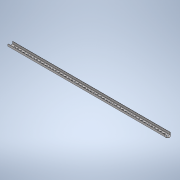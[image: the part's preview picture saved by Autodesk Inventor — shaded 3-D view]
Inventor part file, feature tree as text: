
AUTODESK INVENTOR PART (.ipt)
format: ipt  version: 2022 (Build 260153000, 153)  size: 299,008 bytes
history: native  units: mm
features: sheet_metal_op x4, sketch x4, other x3, extrude x2, pattern_linear x1
ambient origin geometry x8: Origin, YZ Plane, XZ Plane, XY Plane, X Axis, Y Axis, Z Axis, Center Point
bodies: Solid1 (feature_tree)
feature tree (14):
  sheet_metal_op  "Face1"
  sheet_metal_op  "Flange1"
  extrude  "Extrusion1"  Depth=30.0mm
  pattern_linear  "Rectangular Pattern1"  Spacing1=3.0mm  [1 undecoded]
  extrude  "Extrusion2"  Depth=1.5mm
  sketch  "Sketch1"  dims[d0=1000.0mm d1=30.0mm]
  other  "Plate1"
  sketch  "Sketch2"  dims[d2=1.5mm]
  other  "Plate2"
  sheet_metal_op  "Bend1"
  sheet_metal_op  "Corner1"
  sketch  "Sketch3"  dims[d3=1.5mm]
  sketch  "Sketch4"  dims[d4=0.75mm d5=3.0mm d6=1.5mm d7=15.0mm d8=90.0deg d9=1.5mm d10=6.0mm d11=1.5mm d12=1.5mm d13=15.0mm d14=15.0mm d15=0.0mm d16=0.0mm d17=490.0mm d19=20.0mm d20=0.0mm d21=0.0mm d22=12.2mm]
  other  "Definition1"
note: 1 required parameter value undecoded (feature->parameter linkage not recoverable at this tier; creation-order binding heuristic only, values carry confidence <= 0.55)
